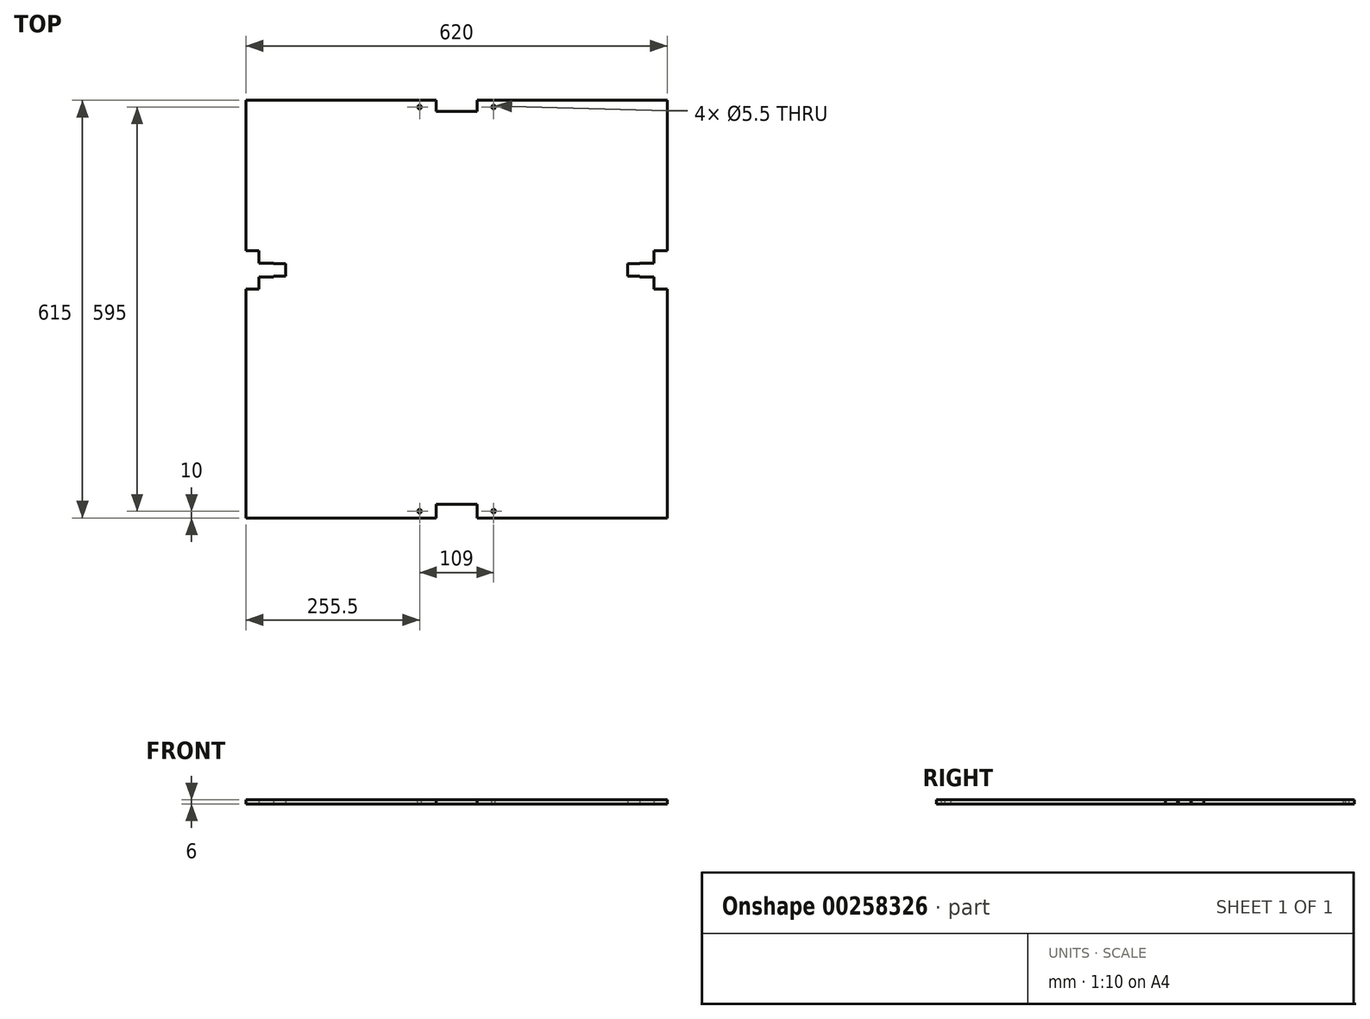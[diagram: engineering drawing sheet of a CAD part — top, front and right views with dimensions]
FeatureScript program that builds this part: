
annotation { "Feature Type Name" : "Feature", "Feature Type Description" : "" }
export const myFeature = defineFeature(function(context is Context, id is Id, definition is map)
    precondition{}
    {
        {
            var Q0;
            Q0=qCreatedBy(makeId("Top.planeOp"),FACE);
            var sketch = newSketch(context, id + "F0", { "sketchPlane" : qUnion([Q0])});
            skLineSegment(sketch, "E0.bottom", {"start": v(310, -307.5) * mm, "end": v(30.2, -307.5) * mm});
            skLineSegment(sketch, "E0.top", {"start": v(310, 307.5) * mm, "end": v(30.2, 307.5) * mm});
            skLineSegment(sketch, "E0.left", {"start": v(310, -307.5) * mm, "end": v(310, 29.3) * mm});
            skLineSegment(sketch, "E0.right", {"start": v(-310, -307.5) * mm, "end": v(-310, 29.3) * mm});
            skPoint(sketch, "E0.middle", {"position": v(0, 0) * mm});
            skLineSegment(sketch, "E1", {"start": v(0, 307.5) * mm, "end": v(0, -307.5) * mm, "construction": true});
            skLineSegment(sketch, "E2", {"start": v(-30.2, 307.5) * mm, "end": v(-30.2, 291.1) * mm});
            skLineSegment(sketch, "E3", {"start": v(-30.2, 291.1) * mm, "end": v(30.2, 291.1) * mm});
            skLineSegment(sketch, "E4", {"start": v(30.2, 291.1) * mm, "end": v(30.2, 307.5) * mm});
            skLineSegment(sketch, "E5.trimOffspring", {"start": v(-30.2, 307.5) * mm, "end": v(-310, 307.5) * mm});
            skLineSegment(sketch, "E6.trimOffspring", {"start": v(-30.2, -307.5) * mm, "end": v(-310, -307.5) * mm});
            skLineSegment(sketch, "E7", {"start": v(-30.2, -307.5) * mm, "end": v(-30.2, -287.1) * mm});
            skLineSegment(sketch, "E8", {"start": v(-30.2, -287.1) * mm, "end": v(30.2, -287.1) * mm});
            skLineSegment(sketch, "E9", {"start": v(30.2, -287.1) * mm, "end": v(30.2, -307.5) * mm});
            skLineSegment(sketch, "E10", {"start": v(-310, 85.7) * mm, "end": v(-290.8, 85.7) * mm});
            skLineSegment(sketch, "E11", {"start": v(-290.8, 85.7) * mm, "end": v(-290.8, 67.7) * mm});
            skLineSegment(sketch, "E12", {"start": v(-269.6, 48.3) * mm, "end": v(-251.6, 48.3) * mm});
            skLineSegment(sketch, "E13", {"start": v(-251.6, 66.7) * mm, "end": v(-251.6, 48.3) * mm});
            skLineSegment(sketch, "E14", {"start": v(-251.6, 66.7) * mm, "end": v(-269.6, 66.7) * mm});
            skLineSegment(sketch, "E15", {"start": v(-290.8, 29.3) * mm, "end": v(-310, 29.3) * mm});
            skLineSegment(sketch, "E16", {"start": v(-269.6, 66.7) * mm, "end": v(-269.6, 67.7) * mm});
            skLineSegment(sketch, "E17", {"start": v(-269.6, 67.7) * mm, "end": v(-290.8, 67.7) * mm});
            skLineSegment(sketch, "E18", {"start": v(-269.6, 48.3) * mm, "end": v(-269.6, 47.3) * mm});
            skLineSegment(sketch, "E19", {"start": v(-269.6, 47.3) * mm, "end": v(-290.8, 47.3) * mm});
            skLineSegment(sketch, "E20.trimOffspring", {"start": v(-290.8, 47.3) * mm, "end": v(-290.8, 29.3) * mm});
            skLineSegment(sketch, "E21.trimOffspring", {"start": v(-310, 85.7) * mm, "end": v(-310, 307.5) * mm});
            skLineSegment(sketch, "E22.MirrorCS", {"start": v(269.6, 48.3) * mm, "end": v(269.6, 47.3) * mm});
            skLineSegment(sketch, "E23.MirrorCS", {"start": v(269.6, 66.7) * mm, "end": v(269.6, 67.7) * mm});
            skLineSegment(sketch, "E24.MirrorCS", {"start": v(269.6, 47.3) * mm, "end": v(290.8, 47.3) * mm});
            skLineSegment(sketch, "E25.MirrorCS", {"start": v(290.8, 29.3) * mm, "end": v(310, 29.3) * mm});
            skLineSegment(sketch, "E26.MirrorCS", {"start": v(269.6, 67.7) * mm, "end": v(290.8, 67.7) * mm});
            skLineSegment(sketch, "E27.MirrorCS", {"start": v(251.6, 66.7) * mm, "end": v(251.6, 48.3) * mm});
            skLineSegment(sketch, "E28.MirrorCS", {"start": v(290.8, 47.3) * mm, "end": v(290.8, 29.3) * mm});
            skLineSegment(sketch, "E29.MirrorCS", {"start": v(310, 85.7) * mm, "end": v(290.8, 85.7) * mm});
            skLineSegment(sketch, "E30.MirrorCS", {"start": v(269.6, 48.3) * mm, "end": v(251.6, 48.3) * mm});
            skLineSegment(sketch, "E31.MirrorCS", {"start": v(251.6, 66.7) * mm, "end": v(269.6, 66.7) * mm});
            skLineSegment(sketch, "E32.MirrorCS", {"start": v(290.8, 85.7) * mm, "end": v(290.8, 67.7) * mm});
            skLineSegment(sketch, "E33.trimOffspring", {"start": v(310, 85.7) * mm, "end": v(310, 307.5) * mm});
            skLineSegment(sketch, "E34", {"start": v(-300, 85.7) * mm, "end": v(-300, 29.3) * mm, "construction": true});
            skLineSegment(sketch, "E35", {"start": v(-251.6, 57.5) * mm, "end": v(-300, 57.5) * mm, "construction": true});
            skSolve(sketch);
        }
        {
            var Q0;
            Q0=qSketchRegion(id+"F0",true);
            extrude(context, id + "F1", {"entities" : qUnion([Q0]), "depth" : 6 * mm});
        }
        {
            var Q0;
            Q0=makeQuery(id+"F1.opExtrude","CAP_FACE",FACE,{"disambiguationData":[OSD([sQuery(id+"F0.wireOp",EDGE,"E0.bottom"),sQuery(id+"F0.wireOp",EDGE,"E0.top"),sQuery(id+"F0.wireOp",EDGE,"E0.left"),sQuery(id+"F0.wireOp",EDGE,"E0.right"),sQuery(id+"F0.wireOp",EDGE,"E2"),sQuery(id+"F0.wireOp",EDGE,"E3"),sQuery(id+"F0.wireOp",EDGE,"E4"),sQuery(id+"F0.wireOp",EDGE,"E5.trimOffspring"),sQuery(id+"F0.wireOp",EDGE,"E6.trimOffspring"),sQuery(id+"F0.wireOp",EDGE,"E7"),sQuery(id+"F0.wireOp",EDGE,"E8"),sQuery(id+"F0.wireOp",EDGE,"E9"),sQuery(id+"F0.wireOp",EDGE,"E10"),sQuery(id+"F0.wireOp",EDGE,"E11"),sQuery(id+"F0.wireOp",EDGE,"E12"),sQuery(id+"F0.wireOp",EDGE,"E13"),sQuery(id+"F0.wireOp",EDGE,"E14"),sQuery(id+"F0.wireOp",EDGE,"E15"),sQuery(id+"F0.wireOp",EDGE,"E16"),sQuery(id+"F0.wireOp",EDGE,"E17"),sQuery(id+"F0.wireOp",EDGE,"E18"),sQuery(id+"F0.wireOp",EDGE,"E19"),sQuery(id+"F0.wireOp",EDGE,"E20.trimOffspring"),sQuery(id+"F0.wireOp",EDGE,"E21.trimOffspring"),sQuery(id+"F0.wireOp",EDGE,"E22.MirrorCS"),sQuery(id+"F0.wireOp",EDGE,"E23.MirrorCS"),sQuery(id+"F0.wireOp",EDGE,"E24.MirrorCS"),sQuery(id+"F0.wireOp",EDGE,"E25.MirrorCS"),sQuery(id+"F0.wireOp",EDGE,"E26.MirrorCS"),sQuery(id+"F0.wireOp",EDGE,"E27.MirrorCS"),sQuery(id+"F0.wireOp",EDGE,"E28.MirrorCS"),sQuery(id+"F0.wireOp",EDGE,"E29.MirrorCS"),sQuery(id+"F0.wireOp",EDGE,"E30.MirrorCS"),sQuery(id+"F0.wireOp",EDGE,"E31.MirrorCS"),sQuery(id+"F0.wireOp",EDGE,"E32.MirrorCS"),sQuery(id+"F0.wireOp",EDGE,"E33.trimOffspring")])],"isStart":false});
            var sketch = newSketch(context, id + "F2", { "sketchPlane" : qUnion([Q0])});
            skLineSegment(sketch, "E36.0", {"start": v(-30.2, -287.1) * mm, "end": v(30.2, -287.1) * mm, "construction": true});
            skLineSegment(sketch, "E36.1", {"start": v(30.2, -287.1) * mm, "end": v(30.2, -307.5) * mm, "construction": true});
            skLineSegment(sketch, "E36.2", {"start": v(-30.2, -307.5) * mm, "end": v(-30.2, -287.1) * mm, "construction": true});
            skLineSegment(sketch, "E36.3", {"start": v(30.2, 291.1) * mm, "end": v(30.2, 307.5) * mm, "construction": true});
            skLineSegment(sketch, "E36.4", {"start": v(-30.2, 291.1) * mm, "end": v(30.2, 291.1) * mm, "construction": true});
            skLineSegment(sketch, "E36.5", {"start": v(-30.2, 307.5) * mm, "end": v(-30.2, 291.1) * mm, "construction": true});
            skLineSegment(sketch, "E37", {"start": v(-54.5, 297.5) * mm, "end": v(54.5, 297.5) * mm, "construction": true});
            skLineSegment(sketch, "E38", {"start": v(0, 291.1) * mm, "end": v(0, 297.5) * mm, "construction": true});
            skCircle(sketch, "E39", {"center": v(-54.5, 297.5) * mm, "radius": 2.75 * mm});
            skCircle(sketch, "E40", {"center": v(54.5, 297.5) * mm, "radius": 2.75 * mm});
            skLineSegment(sketch, "E41", {"start": v(-54.5, -297.5) * mm, "end": v(54.5, -297.5) * mm, "construction": true});
            skLineSegment(sketch, "E42", {"start": v(0, -287.1) * mm, "end": v(0, -297.5) * mm, "construction": true});
            skCircle(sketch, "E43", {"center": v(-54.5, -297.5) * mm, "radius": 2.75 * mm});
            skCircle(sketch, "E44", {"center": v(54.5, -297.5) * mm, "radius": 2.75 * mm});
            skSolve(sketch);
        }
        {
            var Q0;
            Q0 = qSketchRegion(id + "F2", true);
            extrude(context, id + "F3", {"entities" : qUnion([Q0]), "operationType" : NewBodyOperationType.REMOVE, "endBound" : BoundingType.UP_TO_NEXT, "oppositeDirection" : true, "depth" : 25 * mm});
        }
    });
